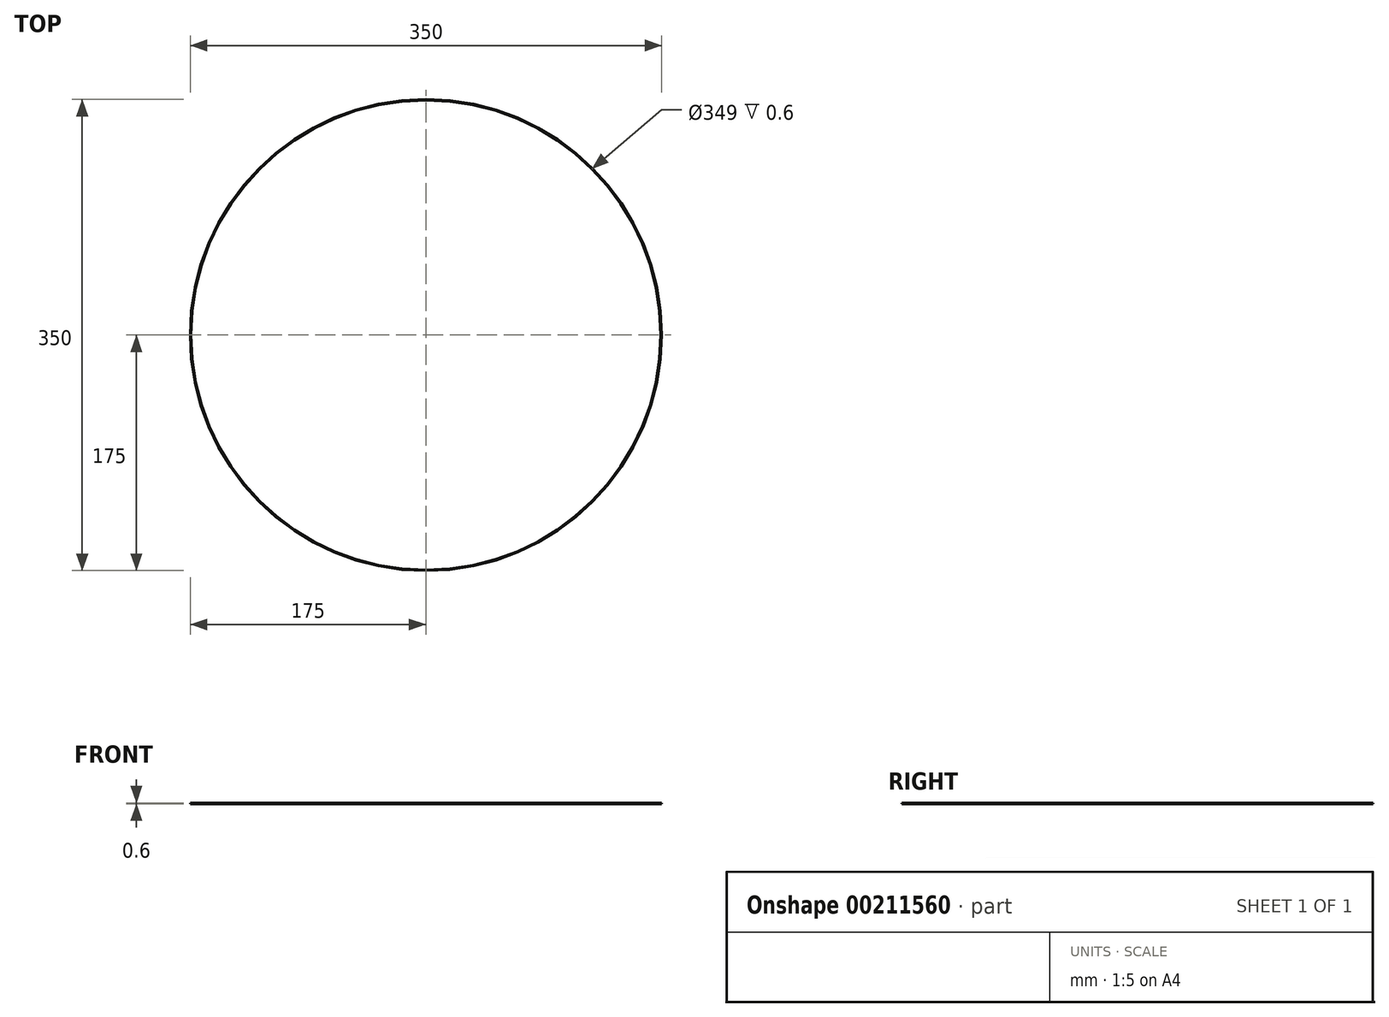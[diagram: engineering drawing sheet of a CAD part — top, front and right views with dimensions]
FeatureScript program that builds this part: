
annotation { "Feature Type Name" : "Feature", "Feature Type Description" : "" }
export const myFeature = defineFeature(function(context is Context, id is Id, definition is map)
    precondition{}
    {
        {
            var Q0;
            Q0=qCreatedBy(makeId("Top.planeOp"),FACE);
            var sketch = newSketch(context, id + "F0", { "sketchPlane" : qUnion([Q0])});
            skCircle(sketch, "E0", {"center": v(0, 0) * mm, "radius": 175 * mm});
            skCircle(sketch, "E1", {"center": v(0, 0) * mm, "radius": 174.5 * mm});
            skSolve(sketch);
        }
        {
            var Q0;
            Q0 = qSketchRegion(id + "F0", true);
            extrude(context, id + "F1", {"entities" : qUnion([Q0]), "depth" : 0.6 * mm});
        }
    });
